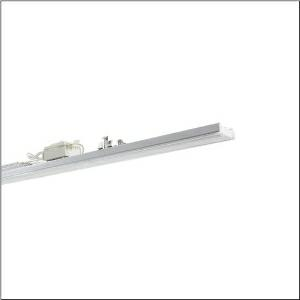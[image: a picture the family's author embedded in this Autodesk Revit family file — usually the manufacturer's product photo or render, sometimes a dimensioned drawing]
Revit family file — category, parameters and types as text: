
# Revit family: licross_r__11_recessed_extreme_mo_51te12dn4axge_e3d7
name_source: partatom
category: Lighting Fixtures
units: mm (PartAtom-declared; Revit-internal decimal feet)

## family parameters
Cut with Voids When Loaded = No
Host = Face
Light Source = No
Part Type = Normal
Room Calculation Point = No
Round Connector Dimension = Use Diameter
Shared = No

## types (1)
- --- (1 x LED, 10240 lm, 56.7 W, 4000K)
    Apparent Load = 57 VA
    CIE Flux Codes = 67 92 99 100 100
    Color Rendering = 80
    Color Temperature = 4000K
    Default Elevation = 1800 mm
    Description = Licross® 11 Recessed extreme MO, luminaire insert, of sheet steel, galvanised, coil coated, white, length: 1.500mm, width: 66mm, height: 67mm, LED rated luminous flux: 10.240lm, light colour: 840, control gear: DALI 2, with plug, 5-pole, with phase selection, mains connection: 220..240V, AC, 50/60Hz, rated input power: 57W, halogen-free wiring, primary optical cover: cover, of PMMA, light emission: direct distribution, primary light characteristic: symmetric, protection rating (complete): IP54, insulation class (complete): insulation class I (protective earthing), certification: CE, ENEC, VDE, UKCA, protection symbol: D if used in an environment with non-conductive dust loads with corresponding accessories, impact resistance: IK06, permissible ambient temperature for indoor applications: -40..+45°C, corresponds to IFS (International Featured Standards) requirements for safety and quality in the food industry, reducing of maximum allowable ambient temperature of 5°C with ceiling mounting, LABS conformity tested according to VDMA 24364:2018-05, packaging unit: 1 piece
    Height = 58 mm
    Lamp = 1 x LED
    Lamp Light Flux = 10240 lm
    Lamp Power = 56.7 W
    Lamp count = 1
    Length = 1500 mm
    Luminous efficacy = 181 lm/W
    Manufacturer = Siteco
    ModVariant = No
    Model = 51TE12DN4AXGE
    Mounting Place = Ceiling
    Mounting Type = Pendant
    Number of Poles = 1
    OnlyDefault = Yes
    Power Factor = 1
    Product Name = Licross® 11 Recessed extreme MO
    Product group = luminaire insert
    ProductGroupID = 902
    Protection Class = Protection class I
    Protection Degree = IP 54
    RLX_Detail_Level = 1
    RLX_Emergency_Light_Flux = 0 lm
    RLX_Emergency_Type = 0
    RLX_Emergency_Type_DB = No
    RlxData = <blob elided: 24417 chars, md5=38a64e18>
    Socket = socket
    Standby Power = 0 W
    System Light Flux = 10240 lm
    System Power = 57 W
    Type Comments = factory setting: luminous flux: 100 % | dim-lin: 254 | 378 mA
    Type Image = l_1296930.jpg
    URL = http://relux.com
    VarID = @adj_082530
    Voltage = 0 V
    Weight = 0.00 kg
    Width = 66 mm

## geometry (parser evidence)
native form markers: Blend x4, Sweep x13
no freeform markers — native parametric forms only
